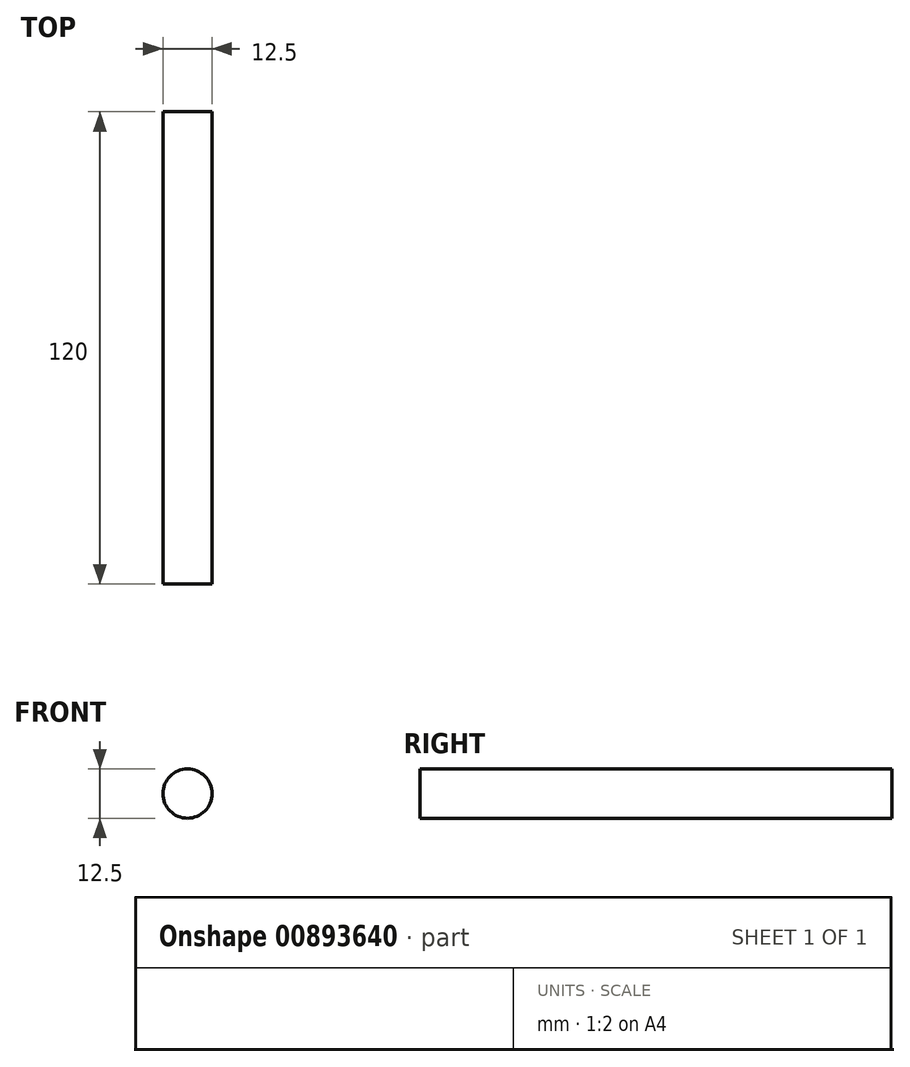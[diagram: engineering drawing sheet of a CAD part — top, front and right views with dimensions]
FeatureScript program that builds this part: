
annotation { "Feature Type Name" : "Feature", "Feature Type Description" : "" }
export const myFeature = defineFeature(function(context is Context, id is Id, definition is map)
    precondition{}
    {
        {
            var Q0;
            Q0=qCreatedBy(makeId("Front.planeOp"),FACE);
            var sketch = newSketch(context, id + "F0", { "sketchPlane" : qUnion([Q0])});
            skCircle(sketch, "E0", {"center": v(0, 0) * mm, "radius": 6.25 * mm});
            skSolve(sketch);
        }
        {
            var Q0;
            Q0 = qSketchRegion(id + "F0", true);
            extrude(context, id + "F1", {"entities" : qUnion([Q0]), "endBound" : BoundingType.SYMMETRIC, "depth" : 120 * mm, "offsetDistance" : 25 * mm});
        }
    });
